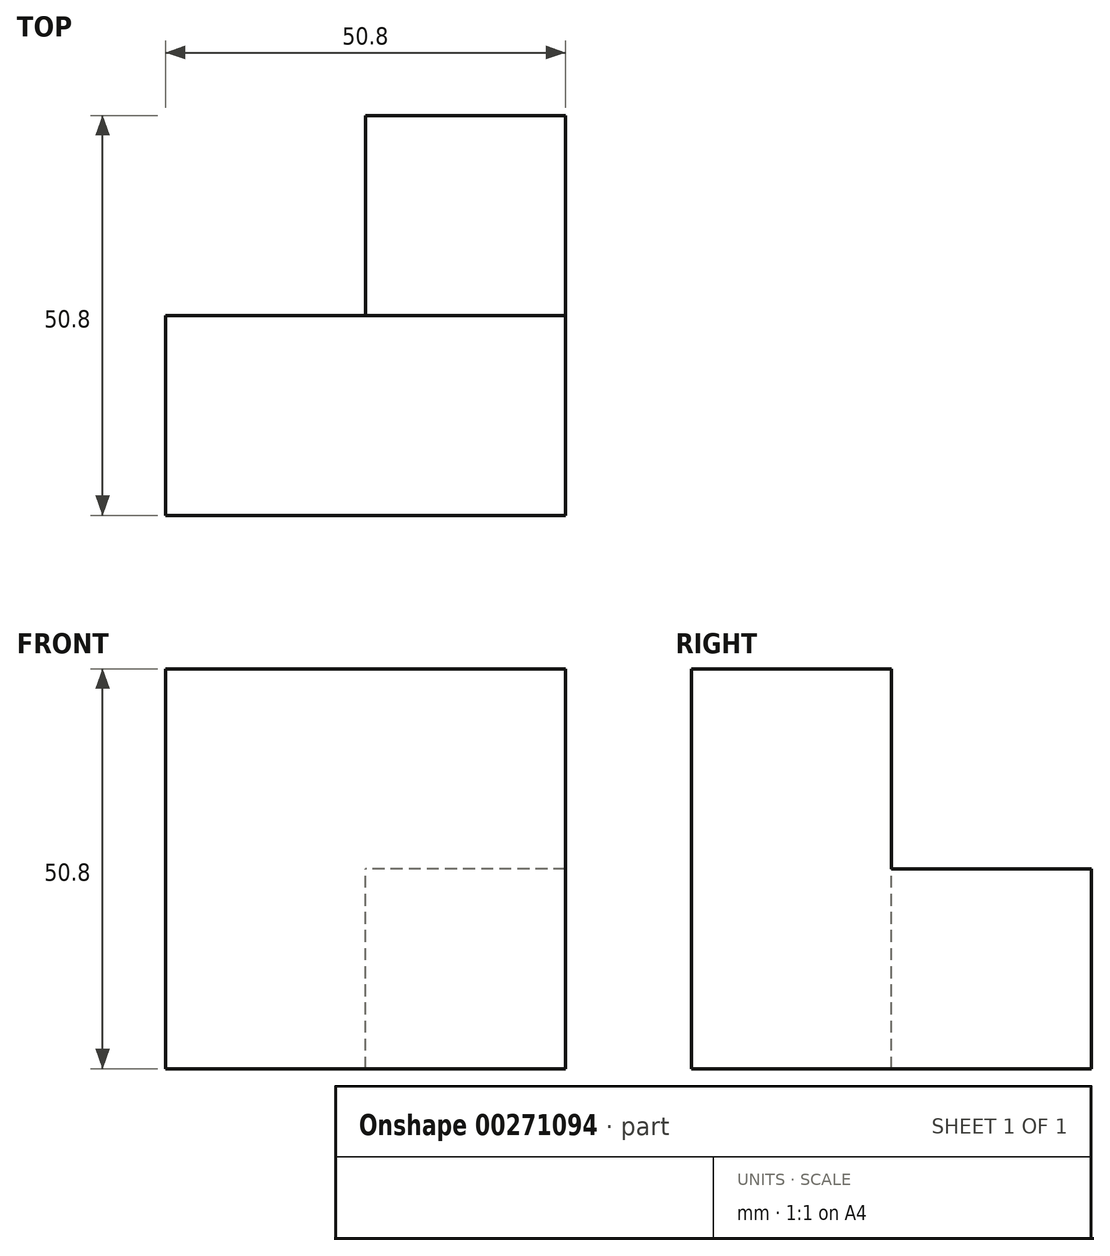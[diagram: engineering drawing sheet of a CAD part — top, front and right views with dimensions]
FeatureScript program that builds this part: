
annotation { "Feature Type Name" : "Feature", "Feature Type Description" : "" }
export const myFeature = defineFeature(function(context is Context, id is Id, definition is map)
    precondition{}
    {
        {
            var Q0;
            Q0=qCreatedBy(makeId("Front.planeOp"),FACE);
            var sketch = newSketch(context, id + "F0", { "sketchPlane" : qUnion([Q0])});
            skLineSegment(sketch, "E0.bottom", {"start": v(0, 0) * mm, "end": v(-50.8, 0) * mm});
            skLineSegment(sketch, "E0.top", {"start": v(0, 50.8) * mm, "end": v(-50.8, 50.8) * mm});
            skLineSegment(sketch, "E0.left", {"start": v(0, 0) * mm, "end": v(0, 50.8) * mm});
            skLineSegment(sketch, "E0.right", {"start": v(-50.8, 0) * mm, "end": v(-50.8, 50.8) * mm});
            skSolve(sketch);
        }
        {
            var Q0;
            Q0=qCreatedBy(makeId("Front.planeOp"),FACE);
            var sketch = newSketch(context, id + "F1", { "sketchPlane" : qUnion([Q0])});
            skLineSegment(sketch, "E1.bottom", {"start": v(0, 0) * mm, "end": v(-25.4, 0) * mm});
            skLineSegment(sketch, "E1.top", {"start": v(0, 25.4) * mm, "end": v(-25.4, 25.4) * mm});
            skLineSegment(sketch, "E1.left", {"start": v(0, 0) * mm, "end": v(0, 25.4) * mm});
            skLineSegment(sketch, "E1.right", {"start": v(-25.4, 0) * mm, "end": v(-25.4, 25.4) * mm});
            skSolve(sketch);
        }
        {
            var Q0;
            Q0 = qSketchRegion(id + "F0", true);
            extrude(context, id + "F2", {"entities" : qUnion([Q0]), "depth" : 25.4 * mm});
        }
        {
            var Q0;
            Q0 = qSketchRegion(id + "F1", true);
            extrude(context, id + "F3", {"entities" : qUnion([Q0]), "operationType" : NewBodyOperationType.ADD, "oppositeDirection" : true, "depth" : 25.4 * mm});
        }
    });
